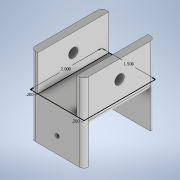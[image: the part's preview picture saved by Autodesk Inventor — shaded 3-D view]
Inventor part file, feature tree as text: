
AUTODESK INVENTOR PART (.ipt)
format: ipt  version: 2020 (Build 240168000, 168)  size: 165,376 bytes
history: native  units: in
note: dims shown in document units (in); Inventor stores cm internally (conversion verified against a paired STEP export)
features: sketch x3, extrude x3, hole x2, fillet x1
ambient origin geometry x8: Origin, YZ Plane, XZ Plane, XY Plane, X Axis, Y Axis, Z Axis, Center Point
bodies: Solid1 (feature_tree)
feature tree (9):
  sketch  "Sketch1"  dims[d0=1.5in d1=2.0in]
  extrude  "Extrusion1"  Depth=2.0in
  extrude  "Extrusion2"  Depth=0.2in
  hole  "Hole1"  [1 undecoded]
  extrude  "Extrusion3"  Depth=0.125in
  hole  "Hole2"  [1 undecoded]
  fillet  "Fillet1"  Radius=1.0in
  sketch  "Sketch2"  dims[d2=0.2in d3=0.2in]
  sketch  "Sketch3"  dims[d4=1.0in d5=0.0in d6=0.2in d7=0.0in d8=0.5in d9=0.266in d10=0.75in d11=0.438in d12=0.25in d13=0.5635in d14=1.0in d15=0.8108in d16=0.5in d17=1.0in d18=0.75in d19=0.125in d20=0.125in d21=1.0in d22=0.0in d23=0.45in d24=0.1125in d25=0.75in d26=0.438in d27=0.25in d28=0.5635in d29=1.0in d30=0.8108in d31=0.125in d32=0.125in d33=0.125in]
note: 2 required parameter values undecoded (feature->parameter linkage not recoverable at this tier; creation-order binding heuristic only, values carry confidence <= 0.55)
